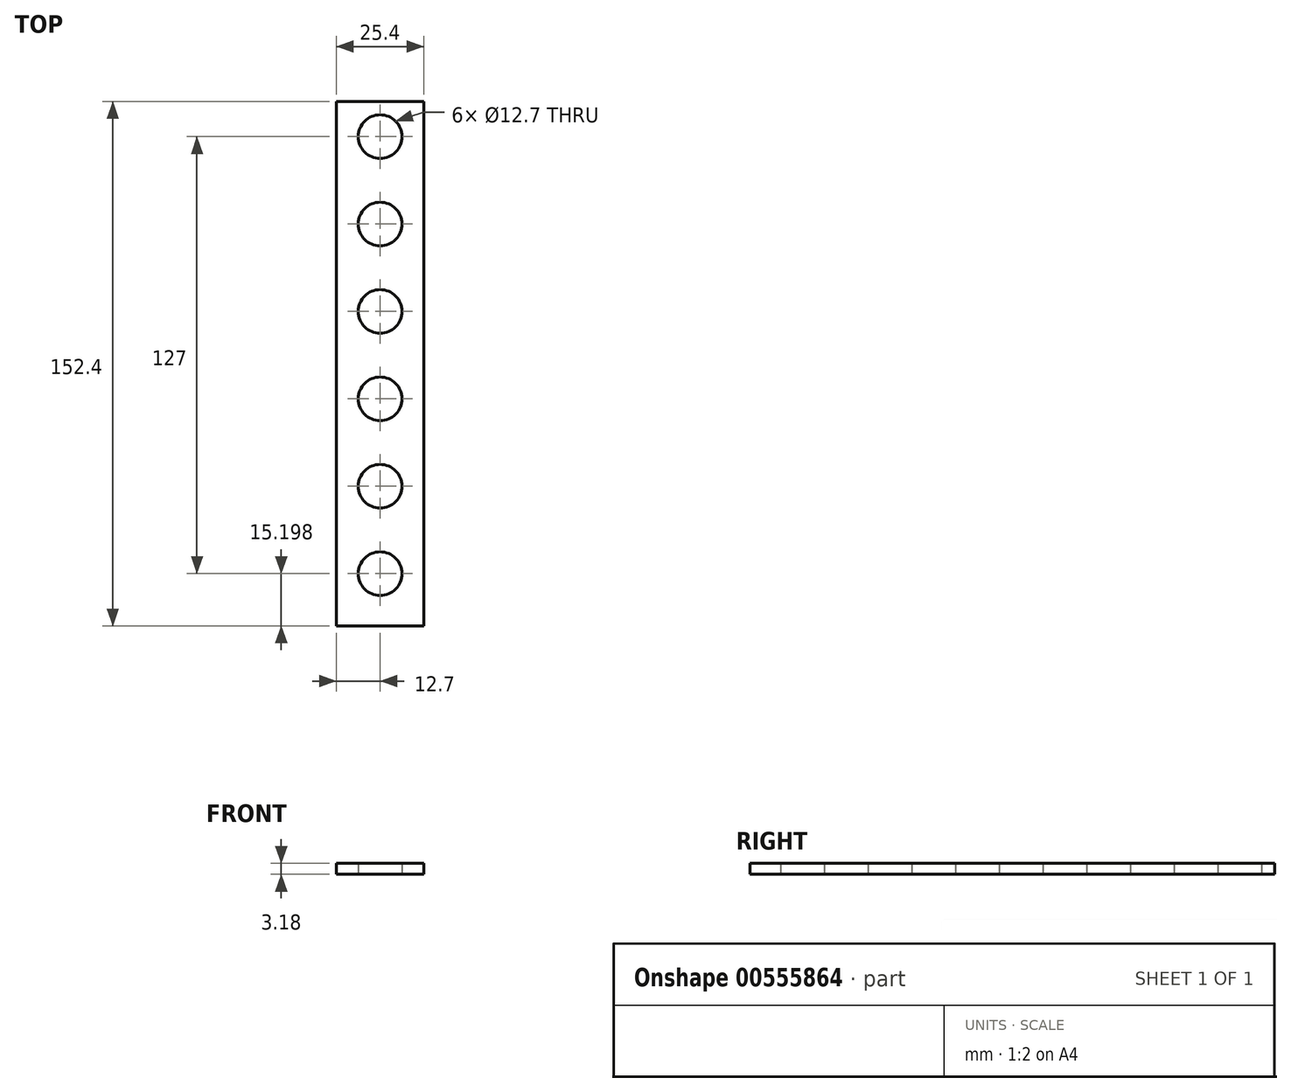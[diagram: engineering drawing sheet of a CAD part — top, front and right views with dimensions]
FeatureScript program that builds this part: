
annotation { "Feature Type Name" : "Feature", "Feature Type Description" : "" }
export const myFeature = defineFeature(function(context is Context, id is Id, definition is map)
    precondition{}
    {
        {
            var Q0;
            Q0=qCreatedBy(makeId("Top.planeOp"),FACE);
            var sketch = newSketch(context, id + "F0", { "sketchPlane" : qUnion([Q0])});
            skLineSegment(sketch, "E0.bottom", {"start": v(-12.7, -76.2) * mm, "end": v(12.7, -76.2) * mm});
            skLineSegment(sketch, "E0.top", {"start": v(-12.7, 76.2) * mm, "end": v(12.7, 76.2) * mm});
            skLineSegment(sketch, "E0.left", {"start": v(-12.7, -76.2) * mm, "end": v(-12.7, 76.2) * mm});
            skLineSegment(sketch, "E0.right", {"start": v(12.7, -76.2) * mm, "end": v(12.7, 76.2) * mm});
            skPoint(sketch, "E0.middle", {"position": v(0, 0) * mm});
            skSolve(sketch);
        }
        {
            var Q0;
            Q0=makeQuery(id+"F0.imprint","IMPRINT",FACE,{"disambiguationData":[TD([[makeQuery(id+"F0.imprint","IMPRINT",EDGE,{"derivedFrom":sQuery(id+"F0.wireOp",EDGE,"E0.bottom")}),1.0]])]});
            extrude(context, id + "F1", {"entities" : qUnion([Q0]), "depth" : 3.17 * mm, "offsetDistance" : 25.4 * mm});
        }
        {
            var Q0;
            Q0=qCreatedBy(makeId("Top.planeOp"),FACE);
            var sketch = newSketch(context, id + "F2", { "sketchPlane" : qUnion([Q0])});
            skCircle(sketch, "E1", {"center": v(0, -137.2) * mm, "radius": 6.35 * mm});
            skCircle(sketch, "E2.0.1.0", {"center": v(0, -111.8) * mm, "radius": 6.35 * mm});
            skLineSegment(sketch, "E2.direction2", {"start": v(0, -137.2) * mm, "end": v(0, -111.8) * mm, "construction": true});
            skCircle(sketch, "E3.0.1.0", {"center": v(0, -86.4) * mm, "radius": 6.35 * mm});
            skLineSegment(sketch, "E3.direction2", {"start": v(0, -111.8) * mm, "end": v(0, -86.4) * mm, "construction": true});
            skCircle(sketch, "E4.0.1.0", {"center": v(0, -61) * mm, "radius": 6.35 * mm});
            skCircle(sketch, "E4.0.1.1", {"center": v(0, -35.6) * mm, "radius": 6.35 * mm});
            skLineSegment(sketch, "E4.0.1.2", {"start": v(0, -61) * mm, "end": v(0, -35.6) * mm, "construction": true});
            skLineSegment(sketch, "E4.0.1.3", {"start": v(0, -35.6) * mm, "end": v(0, -10.2) * mm, "construction": true});
            skCircle(sketch, "E4.0.1.4", {"center": v(0, -10.2) * mm, "radius": 6.35 * mm});
            skLineSegment(sketch, "E4.direction2", {"start": v(0, -137.2) * mm, "end": v(0, -61) * mm, "construction": true});
            skCircle(sketch, "E5.0.1.0", {"center": v(0, 116.8) * mm, "radius": 6.35 * mm});
            skCircle(sketch, "E5.0.1.1", {"center": v(0, 91.4) * mm, "radius": 6.35 * mm});
            skLineSegment(sketch, "E5.0.1.2", {"start": v(0, 40.6) * mm, "end": v(0, 66) * mm, "construction": true});
            skCircle(sketch, "E5.0.1.3", {"center": v(0, 66) * mm, "radius": 6.35 * mm});
            skLineSegment(sketch, "E5.0.1.4", {"start": v(0, 15.2) * mm, "end": v(0, 40.6) * mm, "construction": true});
            skCircle(sketch, "E5.0.1.5", {"center": v(0, 40.6) * mm, "radius": 6.35 * mm});
            skCircle(sketch, "E5.0.1.6", {"center": v(0, 15.2) * mm, "radius": 6.35 * mm});
            skLineSegment(sketch, "E5.0.1.7", {"start": v(0, 15.2) * mm, "end": v(0, 91.4) * mm, "construction": true});
            skCircle(sketch, "E5.0.1.8", {"center": v(0, 142.2) * mm, "radius": 6.35 * mm});
            skLineSegment(sketch, "E5.0.1.9", {"start": v(0, 116.8) * mm, "end": v(0, 142.2) * mm, "construction": true});
            skLineSegment(sketch, "E5.0.1.10", {"start": v(0, 91.4) * mm, "end": v(0, 116.8) * mm, "construction": true});
            skLineSegment(sketch, "E5.direction2", {"start": v(0, -137.2) * mm, "end": v(0, 15.2) * mm, "construction": true});
            skSolve(sketch);
        }
        {
            var Q0;
            Q0=sQuery(id+"F2.wireOp",VERTEX,"E4.0.1.0.center");
            var Q1;
            Q1=makeQuery(id+"F1.opExtrude","SWEPT_BODY",BODY,{"disambiguationData":[OSD([sQuery(id+"F0.wireOp",EDGE,"E0.bottom"),sQuery(id+"F0.wireOp",EDGE,"E0.top"),sQuery(id+"F0.wireOp",EDGE,"E0.left"),sQuery(id+"F0.wireOp",EDGE,"E0.right")])]});
            hole(context, id + "F3", {"style" : HoleStyle.SIMPLE, "endStyle" : HoleEndStyle.BLIND, "oppositeDirection" : true, "holeDiameter" : 12.7 * mm, "holeDepth" : 25.4 * mm, "isTappedThrough" : true, "tappedDepth" : 12.7 * mm, "tapClearance" : 3, "startFromSketch" : true, "locations" : qUnion([Q0]), "scope" : qUnion([Q1])});
        }
        {
            var Q0;
            Q0=sQuery(id+"F2.wireOp",VERTEX,"E4.0.1.1.center");
            var Q1;
            Q1=sQuery(id+"F2.wireOp",VERTEX,"E4.0.1.3.end");
            var Q2;
            Q2=sQuery(id+"F2.wireOp",VERTEX,"E5.0.1.4.start");
            var Q3;
            Q3=sQuery(id+"F2.wireOp",VERTEX,"E5.0.1.2.start");
            var Q4;
            Q4=sQuery(id+"F2.wireOp",VERTEX,"E5.0.1.2.end");
            var Q5;
            Q5=sQuery(id+"F2.wireOp",VERTEX,"E5.0.1.1.center");
            var Q6;
            Q6=sQuery(id+"F2.wireOp",VERTEX,"E5.0.1.9.start");
            var Q7;
            Q7=sQuery(id+"F2.wireOp",VERTEX,"E5.0.1.8.center");
            var Q8;
            Q8=makeQuery(id+"F1.opExtrude","SWEPT_BODY",BODY,{"disambiguationData":[OSD([sQuery(id+"F0.wireOp",EDGE,"E0.bottom"),sQuery(id+"F0.wireOp",EDGE,"E0.top"),sQuery(id+"F0.wireOp",EDGE,"E0.left"),sQuery(id+"F0.wireOp",EDGE,"E0.right")])]});
            hole(context, id + "F4", {"style" : HoleStyle.SIMPLE, "endStyle" : HoleEndStyle.BLIND, "oppositeDirection" : true, "holeDiameter" : 12.7 * mm, "holeDepth" : 25.4 * mm, "isTappedThrough" : true, "tappedDepth" : 12.7 * mm, "tapClearance" : 3, "startFromSketch" : true, "locations" : qUnion([Q0, Q1, Q2, Q3, Q4, Q5, Q6, Q7]), "scope" : qUnion([Q8])});
        }
    });
